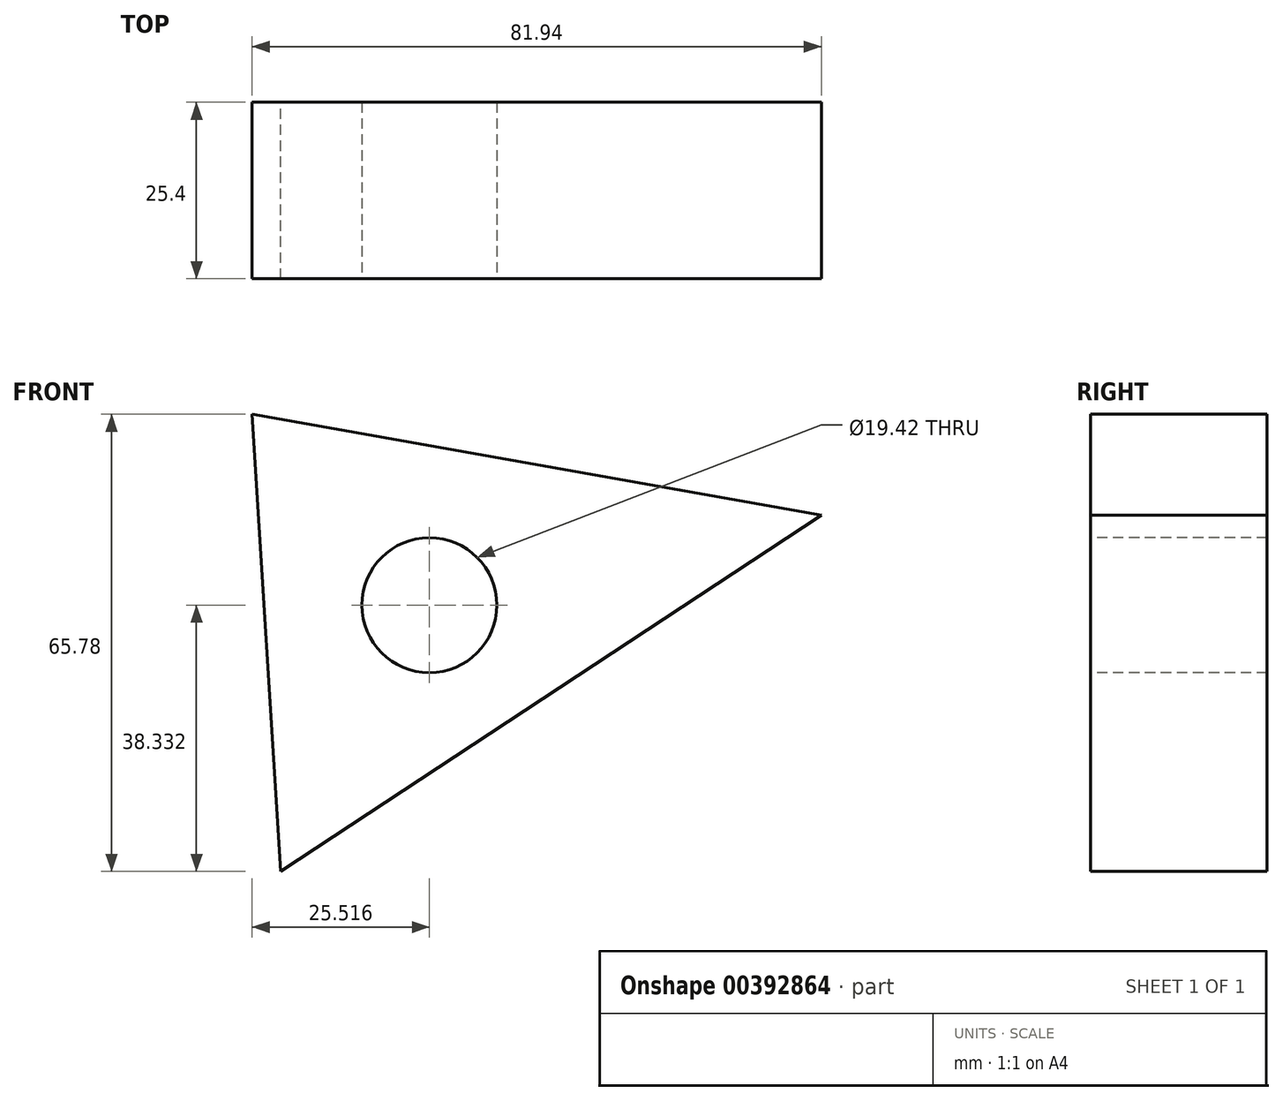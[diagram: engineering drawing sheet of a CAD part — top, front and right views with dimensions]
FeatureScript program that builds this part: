
annotation { "Feature Type Name" : "Feature", "Feature Type Description" : "" }
export const myFeature = defineFeature(function(context is Context, id is Id, definition is map)
    precondition{}
    {
        {
            var Q0;
            Q0=qCreatedBy(makeId("Front.planeOp"),FACE);
            var sketch = newSketch(context, id + "F0", { "sketchPlane" : qUnion([Q0])});
            skLineSegment(sketch, "E0", {"start": v(-60.8, 48.67) * mm, "end": v(-56.68, -17.11) * mm});
            skLineSegment(sketch, "E1", {"start": v(-56.68, -17.11) * mm, "end": v(21.14, 34.16) * mm});
            skLineSegment(sketch, "E2", {"start": v(21.14, 34.16) * mm, "end": v(-60.8, 48.67) * mm});
            skSolve(sketch);
        }
        {
            var Q0;
            Q0 = qSketchRegion(id + "F0", true);
            extrude(context, id + "F1", {"entities" : qUnion([Q0]), "depth" : 25.4 * mm, "offsetDistance" : 25.4 * mm});
        }
        {
            var Q0;
            Q0=makeQuery(id+"F1.opExtrude","CAP_FACE",FACE,{"disambiguationData":[OSD([sQuery(id+"F0.wireOp",EDGE,"E0"),sQuery(id+"F0.wireOp",EDGE,"E1"),sQuery(id+"F0.wireOp",EDGE,"E2")])],"isStart":false});
            var sketch = newSketch(context, id + "F2", { "sketchPlane" : qUnion([Q0])});
            skCircle(sketch, "E3", {"center": v(-35.28, 21.22) * mm, "radius": 9.71 * mm});
            skSolve(sketch);
        }
        {
            var Q0;
            Q0 = qSketchRegion(id + "F2", true);
            extrude(context, id + "F3", {"entities" : qUnion([Q0]), "operationType" : NewBodyOperationType.REMOVE, "oppositeDirection" : true, "depth" : 25.4 * mm, "offsetDistance" : 25.4 * mm});
        }
    });
